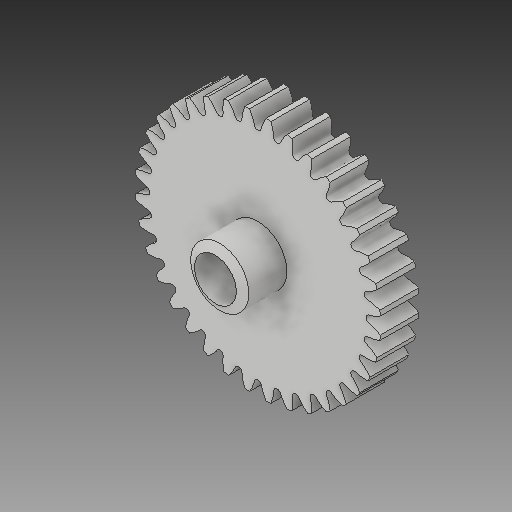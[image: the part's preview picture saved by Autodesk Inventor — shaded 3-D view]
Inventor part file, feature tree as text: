
AUTODESK INVENTOR PART (.ipt)
format: ipt  version: 2017 (Build 210142000, 142)  size: 398,336 bytes
history: native  units: in
note: dims shown in document units (in); Inventor stores cm internally (conversion verified against a paired STEP export)
features: chamfer x1
ambient origin geometry x8: Origin, YZ Plane, XZ Plane, XY Plane, X Axis, Y Axis, Z Axis, Center Point
bodies: Solid1 (feature_tree)
feature tree (1):
  chamfer  "Chamfer1"  [1 undecoded]
note: 1 required parameter value undecoded (feature->parameter linkage not recoverable at this tier; creation-order binding heuristic only, values carry confidence <= 0.55)
